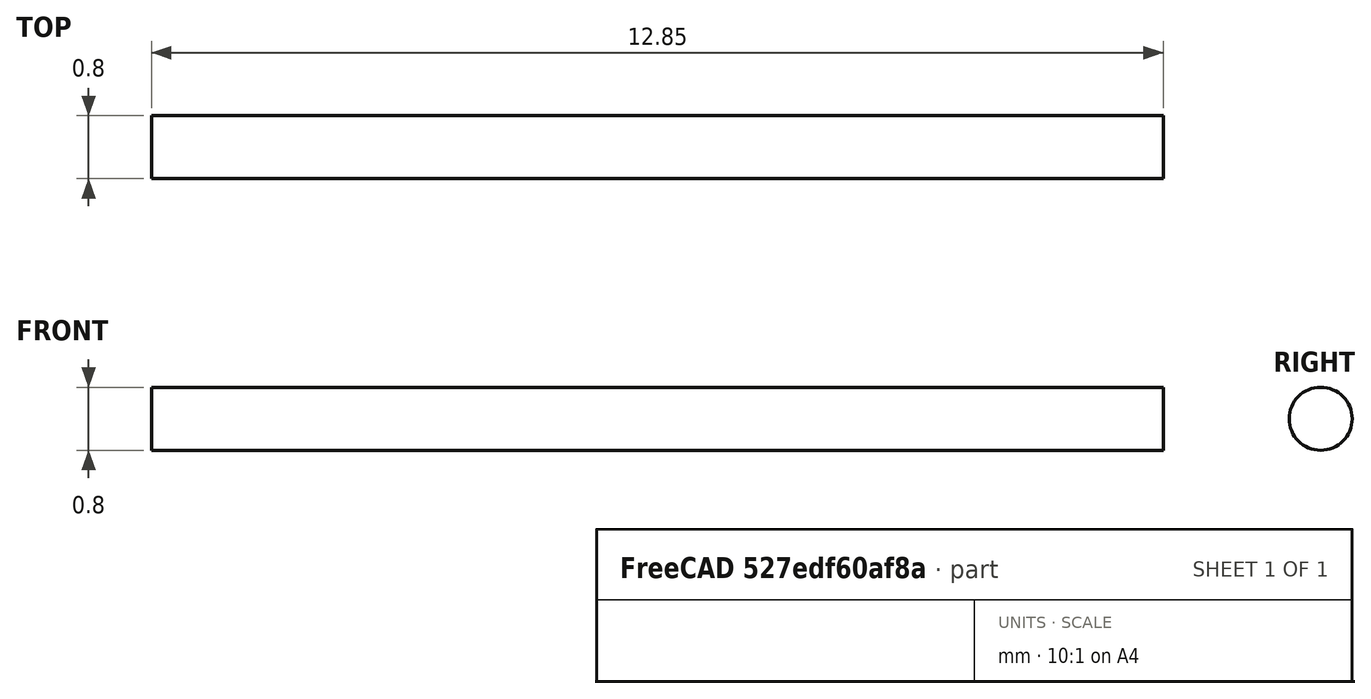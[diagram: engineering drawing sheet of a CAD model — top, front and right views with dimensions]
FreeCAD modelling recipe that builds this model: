
FCSTD DOCUMENT  (FreeCAD 1.0R39109 (Git))
Label: StepperMotor_8mm_i500212644_v3
License: All rights reserved
LicenseURL: https://en.wikipedia.org/wiki/All_rights_reserved
objects: PartDesign::Plane×3, Sketcher::SketchObject×2, PartDesign::Body×2, App::VarSet×1, PartDesign::Pad×1
note: 12 computed .brp shape members not serialized (recipe doc carries the construction recipe); baked Part::Feature solids carry a one-line shape summary decoded from their .brp

FEATURE [Sketcher::SketchObject] Sketch  label="MasterSketch_TOP"
  ArcFitTolerance = 1e-06
  FullyConstrained = true
  MakeInternals = false
  MapMode = 5
  expr: Constraints[10] = VarSet.BodyLength
  expr: Constraints[11] = VarSet.BodyDiameter
  expr: Constraints[14] = VarSet.TotalLength
  expr: Constraints[24] = VarSet.GearDiameter
  expr: Constraints[25] = VarSet.GearLength
  expr: Constraints[36] = VarSet.MountingPlateThickness
  expr: Constraints[48] = VarSet.CappingPlateThickness
  expr: Constraints[58] = VarSet.ShaftThickness
  expr: Constraints[59] = VarSet.ShaftLength
  sketch-geometry (28):
    g0: LineSegment StartX=-4.65 StartY=-4 StartZ=0 EndX=4.65 EndY=-4 EndZ=0
    g1: LineSegment StartX=4.65 StartY=-4 StartZ=0 EndX=4.65 EndY=4 EndZ=0
    g2: LineSegment StartX=4.65 StartY=4 StartZ=0 EndX=-4.65 EndY=4 EndZ=0
    g3: LineSegment StartX=-4.65 StartY=4 StartZ=0 EndX=-4.65 EndY=-4 EndZ=0
    g4: GeomPoint [constr] X=0 Y=0 Z=0
    g5: LineSegment StartX=4.85 StartY=0 StartZ=0 EndX=-8.45 EndY=0 EndZ=0
    g6: LineSegment StartX=-8.45 StartY=1.15 StartZ=0 EndX=-8.45 EndY=-1.15 EndZ=0
    g7: LineSegment StartX=-8.45 StartY=-1.15 StartZ=0 EndX=-5.95 EndY=-1.15 EndZ=0
    g8: LineSegment StartX=-5.95 StartY=-1.15 StartZ=0 EndX=-5.95 EndY=1.15 EndZ=0
    g9: LineSegment StartX=-5.95 StartY=1.15 StartZ=0 EndX=-8.45 EndY=1.15 EndZ=0
    g10: LineSegment StartX=-4.65 StartY=4 StartZ=0 EndX=-5.15 EndY=4 EndZ=0
    g11: LineSegment StartX=-5.15 StartY=4 StartZ=0 EndX=-5.15 EndY=-4 EndZ=0
    g12: LineSegment StartX=-5.15 StartY=-4 StartZ=0 EndX=-4.65 EndY=-4 EndZ=0
    g13: LineSegment StartX=-4.65 StartY=-4 StartZ=0 EndX=-4.65 EndY=4 EndZ=0
    g14: LineSegment StartX=4.65 StartY=4 StartZ=0 EndX=4.65 EndY=-4 EndZ=0
    g15: LineSegment StartX=4.65 StartY=-4 StartZ=0 EndX=4.85 EndY=-4 EndZ=0
    g16: LineSegment StartX=4.85 StartY=-4 StartZ=0 EndX=4.85 EndY=4 EndZ=0
    g17: LineSegment StartX=4.85 StartY=4 StartZ=0 EndX=4.65 EndY=4 EndZ=0
    g18: LineSegment StartX=-8.45 StartY=0.4 StartZ=0 EndX=-8.45 EndY=-0.4 EndZ=0
    g19: LineSegment StartX=-8.45 StartY=-0.4 StartZ=0 EndX=4.4 EndY=-0.4 EndZ=0
    g20: LineSegment StartX=4.4 StartY=-0.4 StartZ=0 EndX=4.4 EndY=0.4 EndZ=0
    g21: LineSegment StartX=4.4 StartY=0.4 StartZ=0 EndX=-8.45 EndY=0.4 EndZ=0
    g22: GeomPoint X=-5.15 Y=0 Z=0
    g23: GeomPoint X=-4.65 Y=0 Z=0
    g24: GeomPoint X=4.65 Y=0 Z=0
    g25: GeomPoint X=-5.95 Y=0 Z=0
    g26: GeomPoint X=4.4 Y=0 Z=0
    g27: GeomPoint X=-8.45 Y=0 Z=0
  constraints (68):
    c: Coincident(g0,g1)
    c: Coincident(g1,g2)
    c: Coincident(g2,g3)
    c: Coincident(g3,g0)
    c: Horizontal(g0)
    c: Horizontal(g2)
    c: Vertical(g1)
    c: Vertical(g3)
    c: Symmetric(g2,g0,g4)
    c: Coincident(g4,g-1)
    c: DistanceX(g0,g0) = 9.3
    c: DistanceY(g3,g3) = 8
    c: PointOnObject(g5,g-1)
    c: PointOnObject(g5,g-1)
    c: DistanceX(g5,g5) = 13.3
    c: Coincident(g6,g7)
    c: Coincident(g7,g8)
    c: Coincident(g8,g9)
    c: Coincident(g9,g6)
    c: Vertical(g6)
    c: Vertical(g8)
    c: Horizontal(g7)
    c: Horizontal(g9)
    c: Symmetric(g6,g6,g5)
    c: DistanceY(g6,g6) = 2.3
    c: DistanceX(g9,g9) = 2.5
    c: Coincident(g10,g11)
    c: Coincident(g11,g12)
    c: Coincident(g12,g13)
    c: Coincident(g13,g10)
    c: Horizontal(g10)
    c: Horizontal(g12)
    c: Vertical(g11)
    c: Vertical(g13)
    c: Coincident(g10,g2)
    c: Horizontal(g11,g0)
    c: DistanceX(g10,g2) = 0.5
    c: Coincident(g14,g15)
    c: Coincident(g15,g16)
    c: Coincident(g16,g17)
    c: Coincident(g17,g14)
    c: Vertical(g14)
    c: Vertical(g16)
    c: Horizontal(g15)
    c: Horizontal(g17)
    c: Coincident(g14,g1)
    c: Horizontal(g15,g0)
    c: PointOnObject(g5,g16)
    c: DistanceX(g17,g17) = 0.2
    c: Coincident(g18,g19)
    c: Coincident(g19,g20)
    c: Coincident(g20,g21)
    c: Coincident(g21,g18)
    c: Vertical(g18)
    c: Vertical(g20)
    c: Horizontal(g19)
    c: Horizontal(g21)
    c: Symmetric(g18,g18,g5)
    c: Distance(g19,g21) = 0.8
    c: DistanceX(g18,g20) = 12.85
    c: Symmetric(g11,g11,g22)
    c: PointOnObject(g23,g5)
    c: Symmetric(g1,g1,g24)
    c: PointOnObject(g23,g3)
    c: Symmetric(g8,g8,g25)
    c: PointOnObject(g26,g5)
    c: PointOnObject(g26,g20)
    c: Coincident(g27,g5)
FEATURE [App::VarSet] VarSet
  BodyDiameter = 8
  BodyLength = 9.3
  CappingPlateThickness = 0.2
  GearDiameter = 2.3
  GearLength = 2.5
  MountingPlateThickness = 0.5
  PinPitch = 1.4
  ShaftLength = 12.85
  ShaftThickness = 0.8
  TotalLength = 13.3
FEATURE [PartDesign::Plane] DatumPlane  label="FrontBodyDatum"
  AttachmentSupport = -> [YZ_Plane,Sketch]
  Length = 60
  MapMode = 53
  Placement = pos=(-4.65,5e-16,-5e-16) rot=(0.57735,0.57735,0.57735;2.0944rad)
  ResizeMode = 0
  Width = 60
FEATURE [PartDesign::Plane] DatumPlane001  label="RearBodyDatum"
  AttachmentSupport = -> [YZ_Plane,Sketch]
  Length = 60
  MapMode = 53
  Placement = pos=(4.65,-5e-16,5e-16) rot=(0.57735,0.57735,0.57735;2.0944rad)
  ResizeMode = 0
  Width = 60
FEATURE [Sketcher::SketchObject] Sketch001
  ArcFitTolerance = 1e-06
  FullyConstrained = true
  MakeInternals = false
  MapMode = 5
  Placement = pos=(-8.45,9e-16,-9e-16) rot=(0.57735,0.57735,0.57735;2.0944rad)
  expr: Constraints[1] = VarSet.ShaftThickness
  sketch-geometry (1):
    g0: Circle CenterX=0 CenterY=0 CenterZ=0 NormalX=0 NormalY=0 NormalZ=1 AngleXU=0 Radius=0.4
  constraints (2):
    c: Coincident(g0,g-1)
    c: Diameter(g0) = 0.8
FEATURE [PartDesign::Pad] Pad
  Direction = (1,0,0)
  Length = 12.85
  Length2 = 10
  Placement = pos=(-8.45,9e-16,-9e-16) rot=(0.57735,0.57735,0.57735;2.0944rad)
  Profile = -> Sketch001
  ReferenceAxis = -> Sketch001 [N_Axis]
  Refine = true
  Suppressed = false
  Type = 0
  expr: Length = VarSet.ShaftLength
FEATURE [PartDesign::Body] Body001  label="Shaft"
  AllowCompound = false
  Group = -> [Sketch001,Pad]
  Origin = -> Origin001
  Tip = -> Pad
FEATURE [PartDesign::Plane] DatumPlane002  label="GearheadDatum"
  AttachmentSupport = -> [Sketch]
  Length = 60
  MapMode = 1
  Placement = pos=(-8.45,0,0) rot=(0.57735,0.57735,0.57735;2.0944rad)
  ResizeMode = 0
  Width = 60
FEATURE [PartDesign::Body] Body  label="Master"
  AllowCompound = false
  Group = -> [Sketch,VarSet,DatumPlane,DatumPlane001,DatumPlane002]
  Origin = -> Origin
